# Revit family: CONV_Flokk_DmstcChrs_RBMNoor6080
name_source: partatom
category: Furniture
revit_build: Autodesk Revit 2015 (Build: 20140606_1530(x64)
units: mm (PartAtom-declared; Revit-internal decimal feet)

## types (1)
- CONV_Flokk_DmstcChrs_RBMNoor6080
    AssetType = Movable
    BIMObjectName = CONV_Flokk_DmstcChrs_RBMNoor6080
    Brand = RBM
    Category = Dining chair
    Collection = RBM Noor
    Color = Various
    ConvergoRefNr = 0119-1802-0035-NO
    Cost = 0 $
    Designer = Form Us With Love
    DurationUnit = Year
    ExpiringDate = 08/2018
    Features = Modular structure
armrests (optional extra), armrest height, armrest width,
seat height, seat depth, lumbar support, tilt resistance/HÅG
inBalance™, lockable tilt and foot support
    HighestSeatingHeight = 476 mm  [stored 1.56168 ft]
    IfcExportAs = IfcFurnishingElementType
    IfcExportType = CHAIR
    LowestSeatingHeight = 476 mm  [stored 1.56168 ft]
    MainColor = Various
    Manufacturer = Flokk
    ManufacturerName = Flokk
    ManufacturerURL = https://www.flokk.com
    Material = Polypropylene, metal, wood
    Model = RBM Noor 6080
    ModelNumber = 6080
    NBSDescription = Domestic chairs
    NBSReference = 45-35-20/365
    Name = DmstcChrs_RBMNoor6080
    NominalDepth = 510 mm  [stored 1.67323 ft]
    NominalHeight = 831 mm  [stored 2.72638 ft]
    NominalLength = 486 mm
    OfficeChairTertiaryMaterial = Plastic, Opaque Black
    ProductInformation = RBM Noor Wooden legs is our most relaxed model in the series. It’s therefore suited to softer surroundings such as gallery spaces, homes or high-end dining areas. A wide range of colours are available for the polypropylene shell, which you can mix-and-match with the wooden legs in natural stained or dark stained ash. Black painted aluminium seat frame is standard but you can also choose polished aluminium.
    SeatingHeight = 476 mm  [stored 1.56168 ft]
    Shape = Sculptured
    Size = 485x510x830 mm
    URL = https://www.flokk.com
    Uniclass2 = Pr_40_50_12_22
    Uniclass2015Description = Dining chairs
    Uniclass2015Reference = Pr_40_50_12_22
    Version = 1
    VersionDate = 14/03/2018
    WarrantyDurationUnit = Year
    Weight = 5.1 kg

note: [stored X ft] marks values corroborated as IEEE doubles in the binary element streams (Revit-internal decimal feet)

## geometry (parser evidence)
native form markers: Blend x4, Sweep x8
no freeform markers — native parametric forms only
